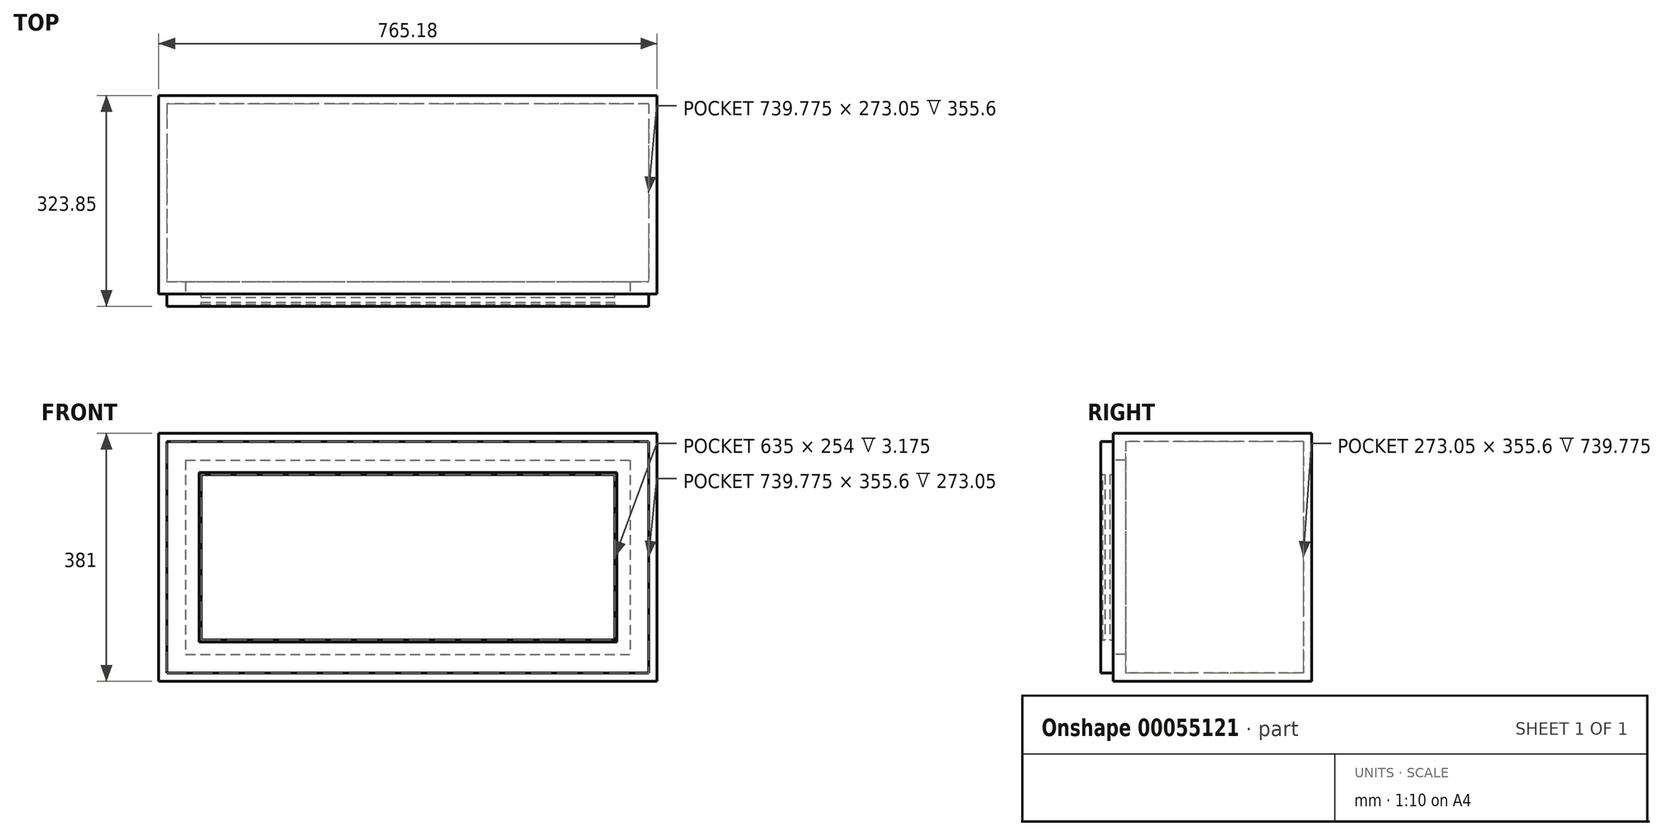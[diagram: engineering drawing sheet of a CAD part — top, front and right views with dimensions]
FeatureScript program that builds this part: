
annotation { "Feature Type Name" : "Feature", "Feature Type Description" : "" }
export const myFeature = defineFeature(function(context is Context, id is Id, definition is map)
    precondition{}
    {
        {
            var Q0;
            Q0=qCreatedBy(makeId("Top.planeOp"),FACE);
            var sketch = newSketch(context, id + "F0", { "sketchPlane" : qUnion([Q0])});
            skLineSegment(sketch, "E0.rect.bottom", {"start": v(382.59, 152.4) * mm, "end": v(-382.59, 152.4) * mm});
            skLineSegment(sketch, "E0.rect.top", {"start": v(382.59, -152.4) * mm, "end": v(-382.59, -152.4) * mm});
            skLineSegment(sketch, "E0.rect.left", {"start": v(382.59, 152.4) * mm, "end": v(382.59, -152.4) * mm});
            skLineSegment(sketch, "E0.rect.right", {"start": v(-382.59, 152.4) * mm, "end": v(-382.59, -152.4) * mm});
            skPoint(sketch, "E0.rect.middle", {"position": v(0, 0) * mm});
            skSolve(sketch);
        }
        {
            var Q0;
            Q0=qSketchRegion(id+"F0",true);
            extrude(context, id + "F1", {"entities" : qUnion([Q0]), "depth" : 381 * mm});
        }
        {
            var Q0;
            Q0=makeQuery(id+"F1.opExtrude","SWEPT_FACE",FACE,{"disambiguationData":[OSD([sQuery(id+"F0.wireOp",EDGE,"E0.rect.top")])]});
            shell(context, id + "F2", {"entities" : qUnion([Q0]), "thickness" : 12.7 * mm});
        }
        {
            var Q0;
            Q0=makeQuery(id+"F1.opExtrude","SWEPT_FACE",FACE,{"disambiguationData":[OSD([sQuery(id+"F0.wireOp",EDGE,"E0.rect.top")])]});
            var sketch = newSketch(context, id + "F3", { "sketchPlane" : qUnion([Q0])});
            skLineSegment(sketch, "E1", {"start": v(-382.59, 0) * mm, "end": v(382.59, 381) * mm, "construction": true});
            skLineSegment(sketch, "E2.rect.bottom", {"start": v(-317.5, 317.5) * mm, "end": v(317.5, 317.5) * mm});
            skLineSegment(sketch, "E2.rect.top", {"start": v(-317.5, 63.5) * mm, "end": v(317.5, 63.5) * mm});
            skLineSegment(sketch, "E2.rect.left", {"start": v(-317.5, 317.5) * mm, "end": v(-317.5, 63.5) * mm});
            skLineSegment(sketch, "E2.rect.right", {"start": v(317.5, 317.5) * mm, "end": v(317.5, 63.5) * mm});
            skPoint(sketch, "E2.rect.middle", {"position": v(0, 190.5) * mm});
            skLineSegment(sketch, "E3.rect.bottom", {"start": v(-341.31, 339.72) * mm, "end": v(341.31, 339.72) * mm});
            skLineSegment(sketch, "E3.rect.top", {"start": v(-341.31, 41.28) * mm, "end": v(341.31, 41.28) * mm});
            skLineSegment(sketch, "E3.rect.left", {"start": v(-341.31, 339.72) * mm, "end": v(-341.31, 41.28) * mm});
            skLineSegment(sketch, "E3.rect.right", {"start": v(341.31, 339.72) * mm, "end": v(341.31, 41.28) * mm});
            skLineSegment(sketch, "E4.rect.bottom", {"start": v(-382.59, 381) * mm, "end": v(382.59, 381) * mm});
            skLineSegment(sketch, "E4.rect.top", {"start": v(-382.59, 0) * mm, "end": v(382.59, 0) * mm});
            skLineSegment(sketch, "E4.rect.left", {"start": v(-382.59, 381) * mm, "end": v(-382.59, 0) * mm});
            skLineSegment(sketch, "E4.rect.right", {"start": v(382.59, 381) * mm, "end": v(382.59, 0) * mm});
            skLineSegment(sketch, "E5.rect.bottom", {"start": v(-374.65, 374.65) * mm, "end": v(374.65, 374.65) * mm});
            skLineSegment(sketch, "E5.rect.top", {"start": v(-374.65, 6.35) * mm, "end": v(374.65, 6.35) * mm});
            skLineSegment(sketch, "E5.rect.left", {"start": v(-374.65, 374.65) * mm, "end": v(-374.65, 6.35) * mm});
            skLineSegment(sketch, "E5.rect.right", {"start": v(374.65, 374.65) * mm, "end": v(374.65, 6.35) * mm});
            skSolve(sketch);
        }
        {
            var Q0;
            Q0=makeQuery(id+"F3.imprint","IMPRINT",FACE,{"disambiguationData":[TD([[makeQuery(id+"F3.imprint","IMPRINT",EDGE,{"derivedFrom":sQuery(id+"F3.wireOp",EDGE,"E4.rect.bottom")}),1.0]])]});
            var Q1;
            Q1=makeQuery(id+"F3.imprint","IMPRINT",FACE,{"disambiguationData":[TD([[makeQuery(id+"F3.imprint","IMPRINT",EDGE,{"derivedFrom":sQuery(id+"F3.wireOp",EDGE,"E5.rect.bottom")}),-1.0]])]});
            var Q2;
            Q2=makeQuery(id+"F3.imprint","IMPRINT",FACE,{"disambiguationData":[TD([[makeQuery(id+"F3.imprint","IMPRINT",EDGE,{"derivedFrom":sQuery(id+"F3.wireOp",EDGE,"E3.rect.bottom")}),1.0]])]});
            extrude(context, id + "F4", {"entities" : qUnion([Q0, Q1, Q2]), "operationType" : NewBodyOperationType.ADD, "oppositeDirection" : true, "depth" : 19.05 * mm});
        }
        {
            var Q0;
            Q0=makeQuery(id+"F3.imprint","IMPRINT",FACE,{"disambiguationData":[TD([[makeQuery(id+"F3.imprint","IMPRINT",EDGE,{"derivedFrom":sQuery(id+"F3.wireOp",EDGE,"E3.rect.bottom")}),1.0]])]});
            var Q1;
            Q1=makeQuery(id+"F3.imprint","IMPRINT",FACE,{"disambiguationData":[TD([[makeQuery(id+"F3.imprint","IMPRINT",EDGE,{"derivedFrom":sQuery(id+"F3.wireOp",EDGE,"E2.rect.bottom")}),1.0]])]});
            extrude(context, id + "F5", {"entities" : qUnion([Q0, Q1]), "operationType" : NewBodyOperationType.ADD, "depth" : 19.05 * mm});
        }
        {
            var Q0;
            Q0=makeQuery(id+"F5.opExtrude","SWEPT_FACE",FACE,{"disambiguationData":[OSD([sQuery(id+"F3.wireOp",EDGE,"E2.rect.right")])]});
            var sketch = newSketch(context, id + "F6", { "sketchPlane" : qUnion([Q0])});
            skLineSegment(sketch, "E6.bottom", {"start": v(157.16, 63.5) * mm, "end": v(165.1, 63.5) * mm});
            skLineSegment(sketch, "E6.top", {"start": v(157.16, 317.5) * mm, "end": v(165.1, 317.5) * mm});
            skLineSegment(sketch, "E6.left", {"start": v(157.16, 63.5) * mm, "end": v(157.16, 317.5) * mm});
            skLineSegment(sketch, "E6.right", {"start": v(165.1, 63.5) * mm, "end": v(165.1, 317.5) * mm});
            skSolve(sketch);
        }
        {
            var Q0;
            Q0 = qSketchRegion(id + "F6", true);
            extrude(context, id + "F7", {"entities" : qUnion([Q0]), "operationType" : NewBodyOperationType.ADD, "endBound" : BoundingType.UP_TO_NEXT, "depth" : 25.4 * mm});
        }
        {
            var Q0;
            Q0=makeQuery(id+"F5.opExtrude","CAP_EDGE",EDGE,{"disambiguationData":[OSD([sQuery(id+"F3.wireOp",EDGE,"E2.rect.top")])],"isStart":false});
            var Q1;
            Q1=makeQuery(id+"F5.opExtrude","CAP_EDGE",EDGE,{"disambiguationData":[OSD([sQuery(id+"F3.wireOp",EDGE,"E2.rect.left")])],"isStart":false});
            var Q2;
            Q2=makeQuery(id+"F5.opExtrude","CAP_EDGE",EDGE,{"disambiguationData":[OSD([sQuery(id+"F3.wireOp",EDGE,"E2.rect.bottom")])],"isStart":false});
            var Q3;
            Q3=makeQuery(id+"F5.opExtrude","CAP_EDGE",EDGE,{"disambiguationData":[OSD([sQuery(id+"F3.wireOp",EDGE,"E2.rect.right")])],"isStart":false});
            chamfer(context, id + "F8", {"entities" : qUnion([Q0, Q1, Q2, Q3]), "width" : 3.17 * mm, "tangentPropagation" : true});
        }
    });
